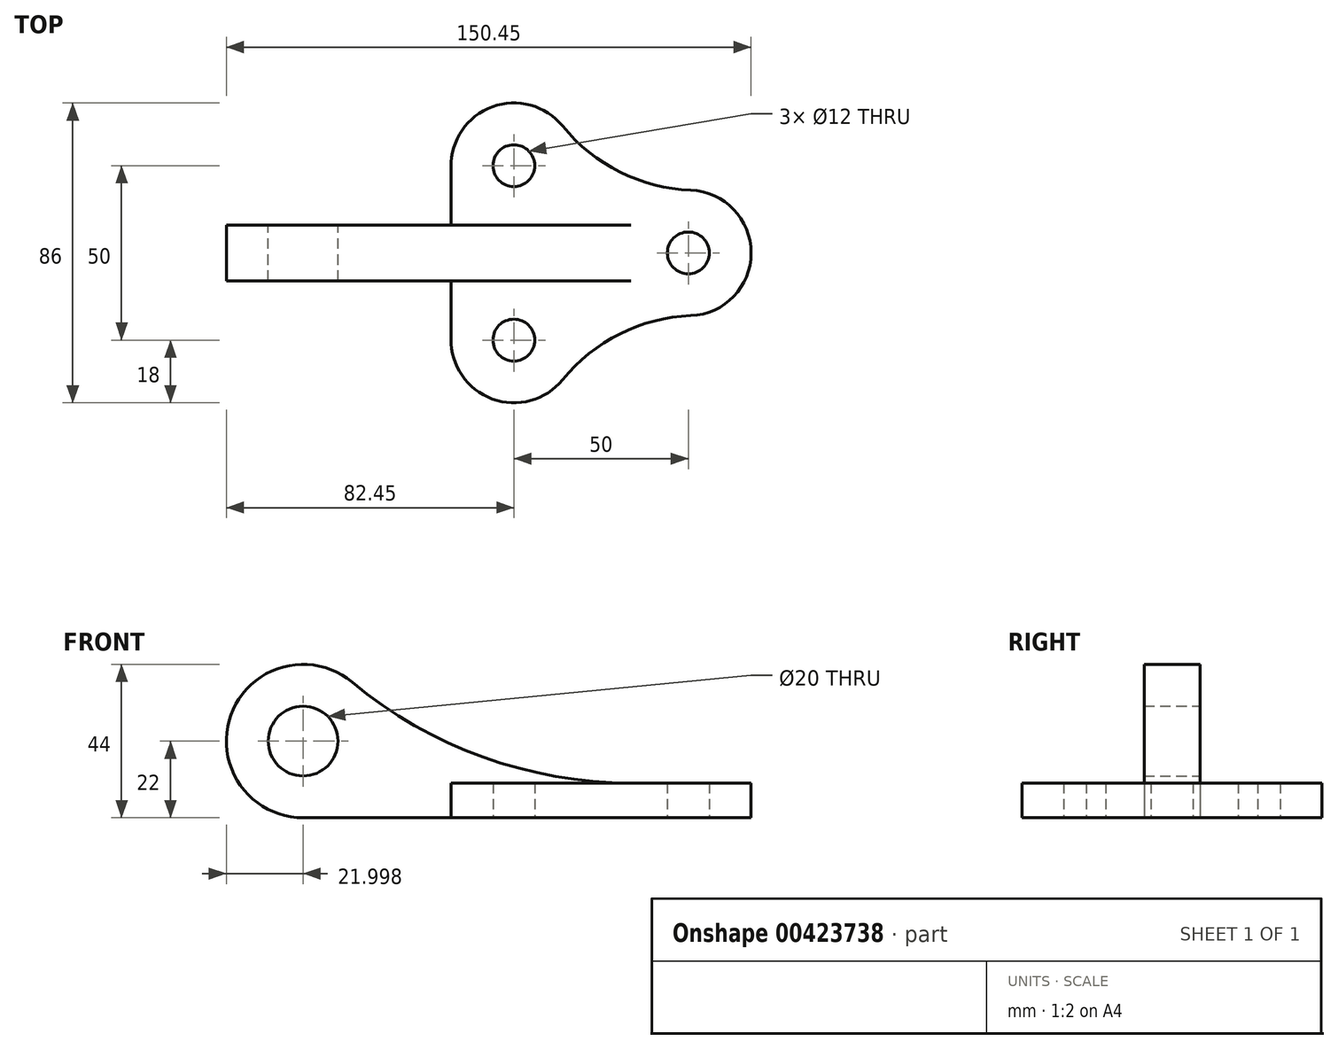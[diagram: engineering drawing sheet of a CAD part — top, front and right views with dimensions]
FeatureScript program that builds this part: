
annotation { "Feature Type Name" : "Feature", "Feature Type Description" : "" }
export const myFeature = defineFeature(function(context is Context, id is Id, definition is map)
    precondition{}
    {
        {
            var Q0;
            Q0=qCreatedBy(makeId("Top.planeOp"),FACE);
            var sketch = newSketch(context, id + "F0", { "sketchPlane" : qUnion([Q0])});
            skCircle(sketch, "E0", {"center": v(0, 0) * mm, "radius": 18 * mm});
            skCircle(sketch, "E1", {"center": v(-50, 25) * mm, "radius": 18 * mm});
            skCircle(sketch, "E2", {"center": v(-50, -25) * mm, "radius": 18 * mm});
            skArc(sketch, "E3", {"start": v(-36.04, 36.37) * mm, "mid": v(-19.64, 23.22) * mm, "end": v(0.72, 17.99) * mm});
            skArc(sketch, "E4", {"start": v(0.72, -17.99) * mm, "mid": v(-19.64, -23.22) * mm, "end": v(-36.04, -36.37) * mm});
            skLineSegment(sketch, "E5", {"start": v(-68, 25.4) * mm, "end": v(-68, -25.4) * mm});
            skCircle(sketch, "E6", {"center": v(-50, 25) * mm, "radius": 6 * mm});
            skCircle(sketch, "E7", {"center": v(-50, -25) * mm, "radius": 6 * mm});
            skCircle(sketch, "E8", {"center": v(0, 0) * mm, "radius": 6 * mm});
            skSolve(sketch);
        }
        {
            var Q0;
            Q0 = qSketchRegion(id + "F0", true);
            extrude(context, id + "F1", {"entities" : qUnion([Q0]), "depth" : 10 * mm});
        }
        {
            var Q0;
            Q0=qCreatedBy(makeId("Front.planeOp"),FACE);
            var sketch = newSketch(context, id + "F2", { "sketchPlane" : qUnion([Q0])});
            skArc(sketch, "E9", {"start": v(-96.38, 38.91) * mm, "mid": v(-131.14, 29.48) * mm, "end": v(-110.45, 0) * mm});
            skArc(sketch, "E10", {"start": v(-96.38, 38.91) * mm, "mid": v(-58.94, 17.45) * mm, "end": v(-16.43, 10) * mm});
            skCircle(sketch, "E11", {"center": v(-110.45, 22) * mm, "radius": 10 * mm});
            skLineSegment(sketch, "E12", {"start": v(-16.43, 10) * mm, "end": v(-16.43, 0) * mm});
            skLineSegment(sketch, "E13", {"start": v(-16.43, 0) * mm, "end": v(-110.45, 0) * mm});
            skSolve(sketch);
        }
        {
            var Q0;
            Q0 = qSketchRegion(id + "F2", true);
            extrude(context, id + "F3", {"entities" : qUnion([Q0]), "operationType" : NewBodyOperationType.ADD, "endBound" : BoundingType.SYMMETRIC, "depth" : 16 * mm});
        }
    });
